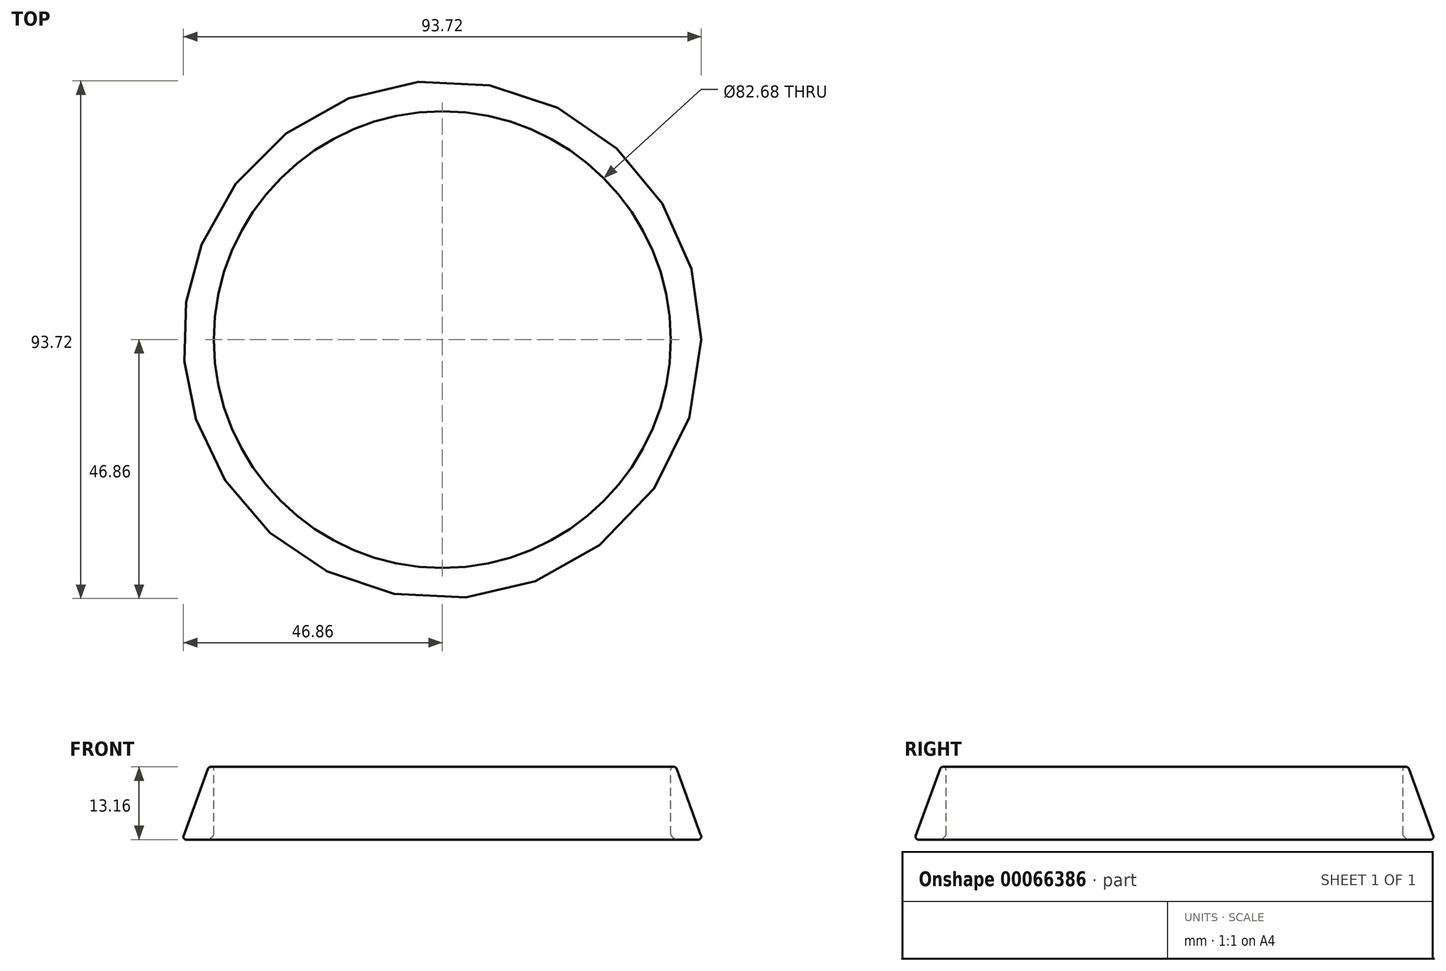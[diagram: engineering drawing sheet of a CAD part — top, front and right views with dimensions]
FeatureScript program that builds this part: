
annotation { "Feature Type Name" : "Feature", "Feature Type Description" : "" }
export const myFeature = defineFeature(function(context is Context, id is Id, definition is map)
    precondition{}
    {
        {
            var Q0;
            Q0=qCreatedBy(makeId("Right.planeOp"),FACE);
            var sketch = newSketch(context, id + "F0", { "sketchPlane" : qUnion([Q0])});
            skLineSegment(sketch, "E0.bottom", {"start": v(42.31, 0) * mm, "end": v(46.35, 0) * mm});
            skLineSegment(sketch, "E0.top", {"start": v(41.85, 13.16) * mm, "end": v(41.93, 13.16) * mm});
            skLineSegment(sketch, "E0.left", {"start": v(41.34, 0.97) * mm, "end": v(41.34, 12.65) * mm});
            skLineSegment(sketch, "E1", {"start": v(46.83, 0.68) * mm, "end": v(42.4, 12.82) * mm});
            skLineSegment(sketch, "E2.0", {"start": v(41.34, 0.76) * mm, "end": v(47, 0.76) * mm});
            skLineSegment(sketch, "E3", {"start": v(41.49, 0.61) * mm, "end": v(41.95, 0.15) * mm});
            skPoint(sketch, "E4.orphan", {"position": v(41.34, 0) * mm});
            skPoint(sketch, "E5.visualSharp", {"position": v(42.29, 13.16) * mm});
            skArc(sketch, "E5.filletArc", {"start": v(42.4, 12.82) * mm, "mid": v(42.22, 13.07) * mm, "end": v(41.93, 13.16) * mm});
            skPoint(sketch, "E6.visualSharp", {"position": v(41.34, 13.16) * mm});
            skArc(sketch, "E6.filletArc", {"start": v(41.85, 13.16) * mm, "mid": v(41.49, 13) * mm, "end": v(41.34, 12.65) * mm});
            skPoint(sketch, "E7.visualSharp", {"position": v(41.34, 0.76) * mm});
            skArc(sketch, "E7.filletArc", {"start": v(41.34, 0.97) * mm, "mid": v(41.38, 0.78) * mm, "end": v(41.49, 0.61) * mm});
            skPoint(sketch, "E8.visualSharp", {"position": v(42.1, 0) * mm});
            skArc(sketch, "E8.filletArc", {"start": v(41.95, 0.15) * mm, "mid": v(42.12, 0.04) * mm, "end": v(42.31, 0) * mm});
            skPoint(sketch, "E9.visualSharp", {"position": v(47.07, 0) * mm});
            skArc(sketch, "E9.filletArc", {"start": v(46.35, 0) * mm, "mid": v(46.77, 0.22) * mm, "end": v(46.83, 0.68) * mm});
            skLineSegment(sketch, "E10", {"start": v(0, 67.7) * mm, "end": v(0, -30.29) * mm, "construction": true});
            skSolve(sketch);
        }
        {
            var Q0;
            Q0=qCreatedBy(makeId("Right.planeOp"),FACE);
            var sketch = newSketch(context, id + "F1", { "sketchPlane" : qUnion([Q0])});
            skLineSegment(sketch, "E11", {"start": v(0, 37.23) * mm, "end": v(0, -27.7) * mm, "construction": true});
            skSolve(sketch);
        }
        {
            var Q0;
            Q0 = qSketchRegion(id + "F0", true);
            var Q1;
            Q1=sQuery(id+"F1.wireOp",EDGE,"E11");
            revolve(context, id + "F2", {"entities" : qUnion([Q0]), "axis" : qUnion([Q1]), "revolveType" : RevolveType.FULL});
        }
    });
